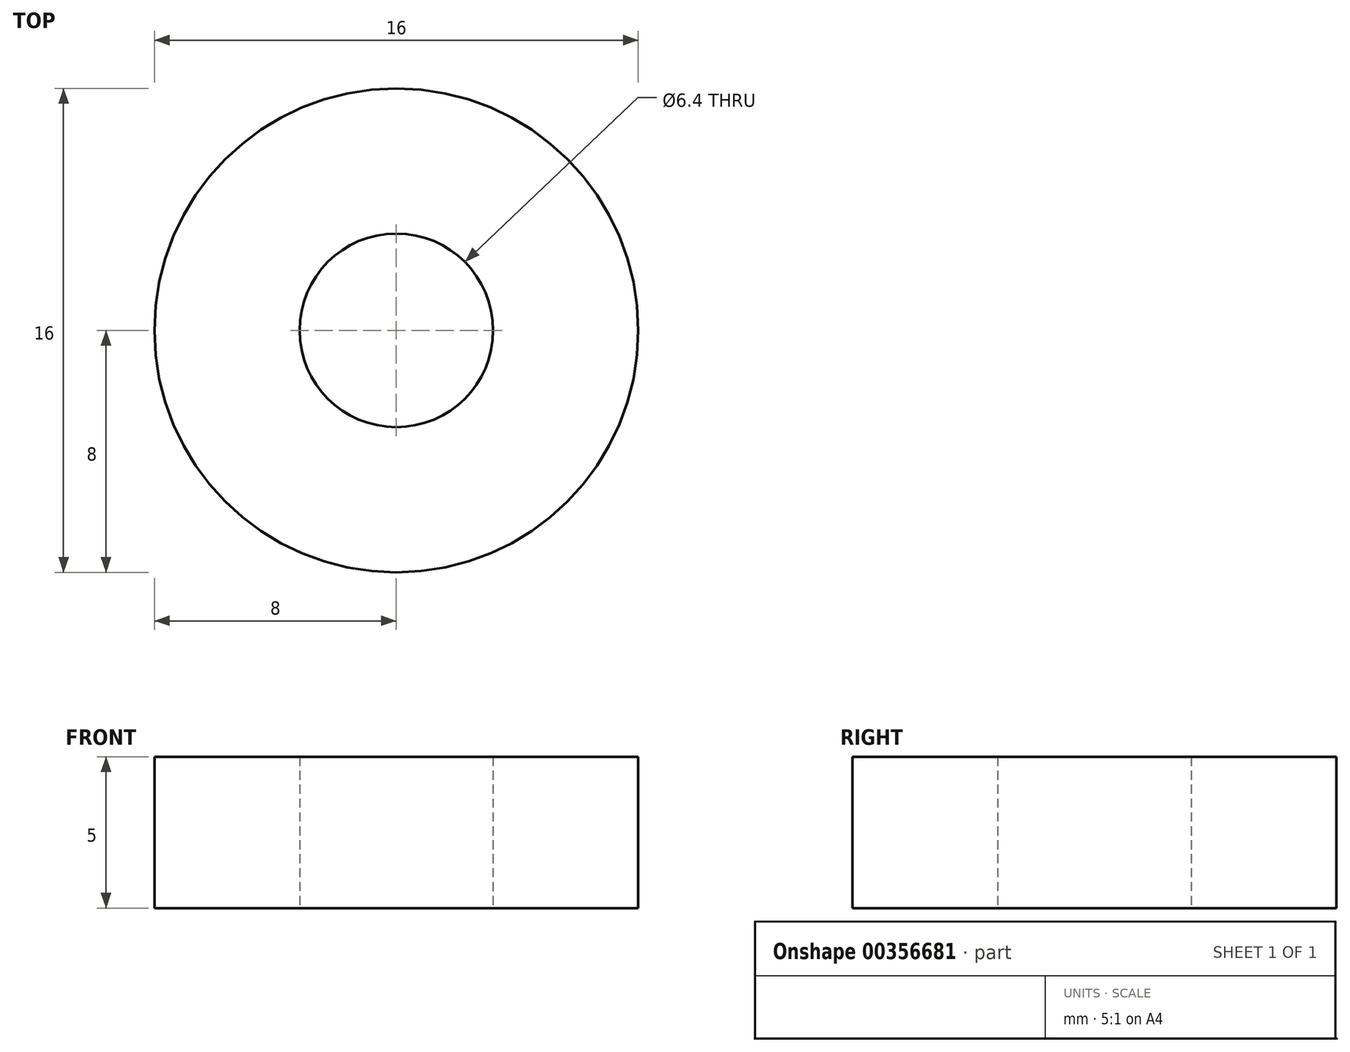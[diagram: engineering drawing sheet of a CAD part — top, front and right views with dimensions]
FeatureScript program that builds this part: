
annotation { "Feature Type Name" : "Feature", "Feature Type Description" : "" }
export const myFeature = defineFeature(function(context is Context, id is Id, definition is map)
    precondition{}
    {
        {
            var Q0;
            Q0=qCreatedBy(makeId("Top.planeOp"),FACE);
            var sketch = newSketch(context, id + "F0", { "sketchPlane" : qUnion([Q0])});
            skCircle(sketch, "E0", {"center": v(0, 0) * mm, "radius": 8 * mm});
            skCircle(sketch, "E1", {"center": v(0, 0) * mm, "radius": 3.2 * mm});
            skSolve(sketch);
        }
        {
            var Q0;
            Q0=makeQuery(id+"F0.imprint","IMPRINT",FACE,{"disambiguationData":[TD([[makeQuery(id+"F0.imprint","IMPRINT",EDGE,{"derivedFrom":sQuery(id+"F0.wireOp",EDGE,"E0")}),1.0]])]});
            extrude(context, id + "F1", {"entities" : qUnion([Q0]), "depth" : 5 * mm});
        }
    });
